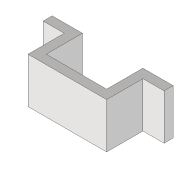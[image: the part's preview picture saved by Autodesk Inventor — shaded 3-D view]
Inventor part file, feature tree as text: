
AUTODESK INVENTOR PART (.ipt)
format: ipt  version: 2020 (Build 240168000, 168)  size: 123,904 bytes
history: native  units: mm
features: extrude x4, sketch x4
ambient origin geometry x8: Origin, YZ Plane, XZ Plane, XY Plane, X Axis, Y Axis, Z Axis, Center Point
bodies: Volumenkörper1 (feature_tree)
feature tree (8):
  extrude  "Extrusion1"  Depth=30.0mm
  extrude  "Extrusion2"  Depth=200.0mm
  extrude  "Extrusion3"  Depth=150.0mm
  extrude  "Extrusion4"  Depth=260.0mm
  sketch  "Skizze1"  dims[d0=30.0mm d1=30.0mm]
  sketch  "Skizze2"  dims[d3=30.0mm d4=200.0mm]
  sketch  "Skizze3"  dims[d5=100.0mm d6=150.0mm]
  sketch  "Skizze4"  dims[d7=150.0mm d8=0.0mm d9=260.0mm d10=30.0mm d11=150.0mm d12=55.0mm d13=300.0mm d14=0.0mm d15=30.0mm d16=400.0mm d17=0.0mm d18=40.0mm d19=20.0mm d20=345.0mm d21=0.0mm d22=0.0mm d23=0.0mm]
